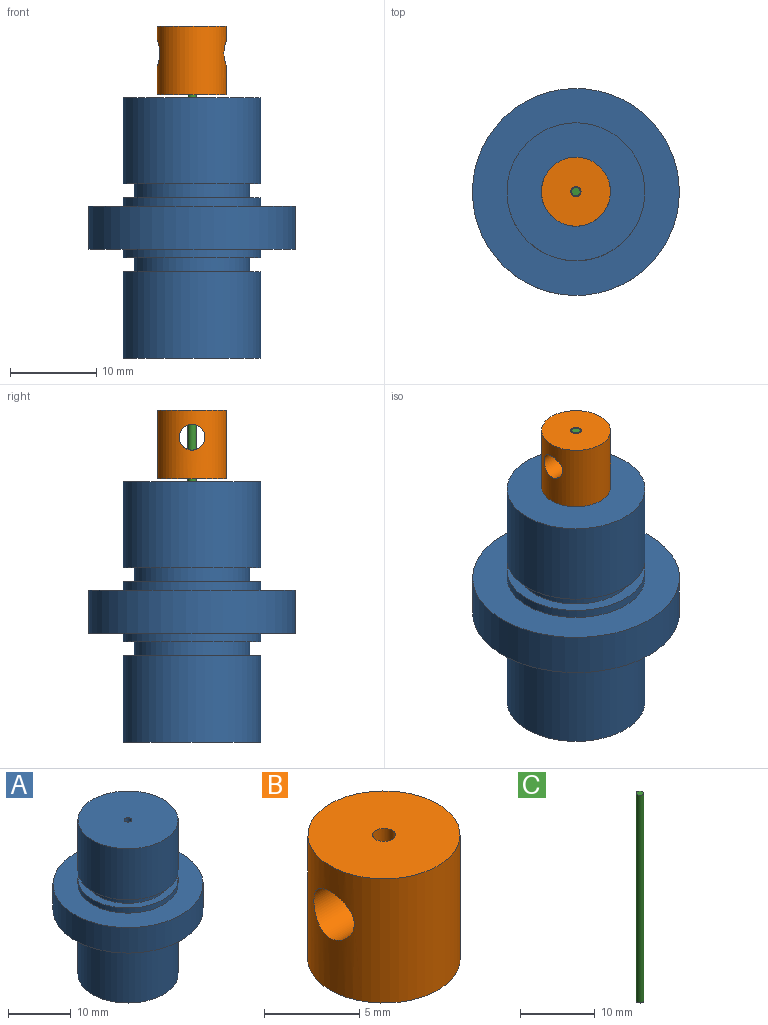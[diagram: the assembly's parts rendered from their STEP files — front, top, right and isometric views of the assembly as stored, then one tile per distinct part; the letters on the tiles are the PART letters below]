
ASSEMBLY  parts=3 mates=4
PART A: 18 faces, bbox 24x24x30.2 mm
  f0: plane 8x8mm, normal (0,0,-1), area 49.1mm2, adj f1,f17
  f1: cylinder r=4mm len=25.2mm, axis (0,0,1), area 633.3mm2, adj f0,f2
  f2: plane 16x16mm, normal (0,0,-1), area 150.8mm2, adj f1,f3
  f3: cylinder r=8mm len=16mm, axis (0,0,1), area 502.7mm2, adj f2,f4
  f4: plane 16x16mm, normal (0,0,1), area 60mm2, adj f3,f5
  f5: cylinder r=6.7mm len=13.4mm, axis (0,0,1), area 67.4mm2, adj f4,f6
  f6: plane 16x16mm, normal (0,0,-1), area 60mm2, adj f5,f7
  f7: cylinder r=8mm len=16mm, axis (0,0,1), area 50.3mm2, adj f6,f8
  f8: plane 24x24mm, normal (0,0,-1), area 251.3mm2, adj f7,f9
  f9: cylinder r=12mm len=24mm, axis (0,0,1), area 377mm2, adj f8,f10
  f10: plane 24x24mm, normal (0,0,1), area 251.3mm2, adj f9,f11
  f11: cylinder r=8mm len=16mm, axis (0,0,1), area 50.3mm2, adj f10,f12
  f12: plane 16x16mm, normal (0,0,1), area 60mm2, adj f11,f13
  f13: cylinder r=6.7mm len=13.4mm, axis (0,0,1), area 67.4mm2, adj f12,f14
  f14: plane 16x16mm, normal (0,0,-1), area 60mm2, adj f13,f15
  f15: cylinder r=8mm len=16mm, axis (0,0,1), area 502.7mm2, adj f14,f16
  f16: plane 16x16mm, normal (0,0,1), area 199.9mm2, adj f15,f17
  f17: cylinder r=0.6mm len=5mm, axis (0,0,1), area 18.8mm2, adj f0,f16
PART B: 8 faces, bbox 8x8x8 mm
  f0: cylinder r=0.6mm len=1.78mm, axis (0,0,-1), area 6.5mm2, adj f1,f7
  f1: plane 8x8mm, normal (0,0,1), area 49.1mm2, adj f0,f6
  f2: cylinder r=0.6mm len=1.78mm, axis (0,0,-1), area 6.5mm2, adj f3,f7
  f3: plane 6x6mm, normal (0,0,-1), area 27.1mm2, adj f2,f4
  f4: cylinder r=3mm len=6mm, axis (0,0,-1), area 32mm2, adj f3,f5
  f5: plane 8x8mm, normal (0,0,-1), area 22mm2, adj f4,f6
  f6: cylinder r=4mm len=8mm, axis (0,0,-1), area 186.7mm2, adj f1,f5,f7
  f7: cylinder r=1.5mm len=8mm, axis (1,0,0), area 70.4mm2, adj f0,f2,f6
PART C: 3 faces, bbox 1x1x34 mm
  f0: cylinder r=0.5mm len=34mm, axis (0,0,-1), area 106.8mm2, adj f1,f2
  f1: plane 1x1mm, normal (0,0,1), area 0.8mm2, adj f0
  f2: plane 1x1mm, normal (0,0,-1), area 0.8mm2, adj f0
PLACE A t=(-3.08,-10.12,7.9)mm
PLACE B t=(-3.08,-10.12,13.2)mm
PLACE C t=(-3.08,-10.12,-12.8)mm
MATE slider C.f0 <-> A.f1  axis (0,0,-1) through (-3.08,-10.12,4.2)mm
MATE fastened A.f1 <-> B.f0  axis (0,0,1) through (-3.08,-10.12,12.9)mm
MATE cylindrical C.f0 <-> B.f0  axis (0,0,1) through (-3.08,-10.12,21.2)mm
MATE fastened B.f0 <-> C.f0  axis (0,0,1) through (-3.08,-10.12,21.2)mm
